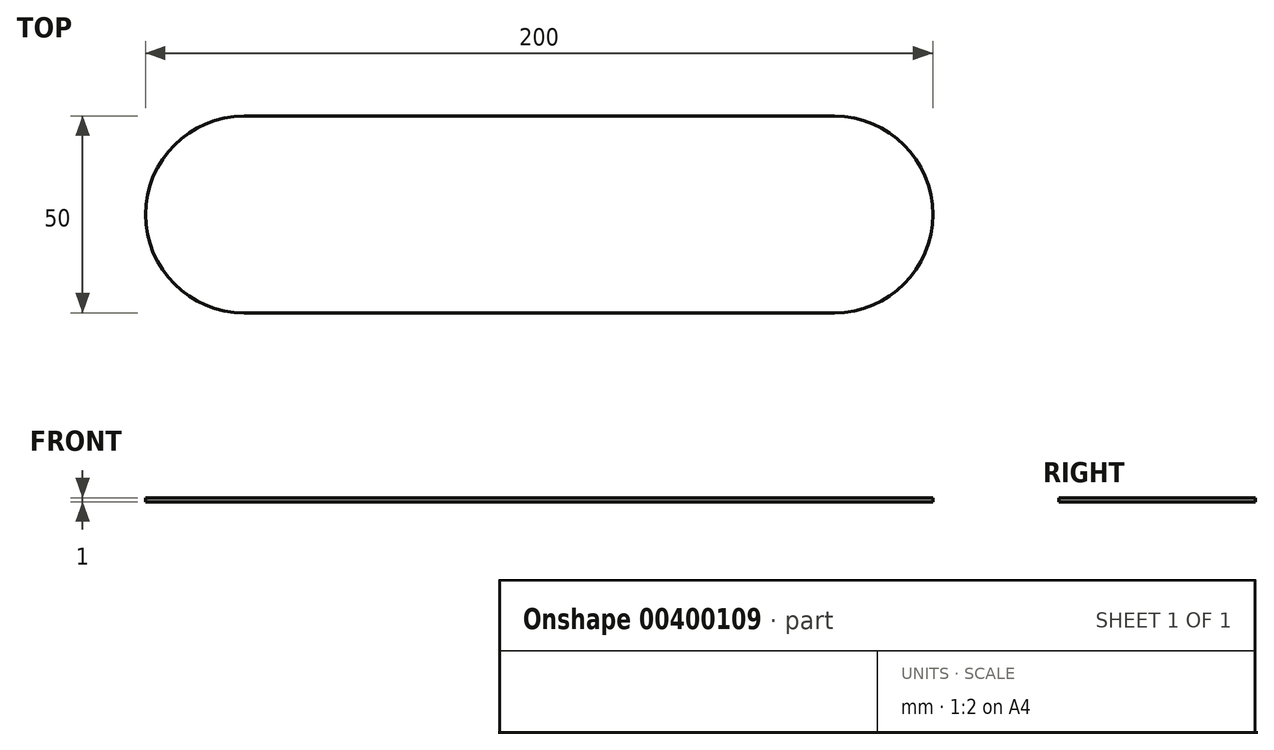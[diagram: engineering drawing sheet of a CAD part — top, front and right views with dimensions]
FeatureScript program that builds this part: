
annotation { "Feature Type Name" : "Feature", "Feature Type Description" : "" }
export const myFeature = defineFeature(function(context is Context, id is Id, definition is map)
    precondition{}
    {
        {
            var Q0;
            Q0=qCreatedBy(makeId("Top.planeOp"),FACE);
            var sketch = newSketch(context, id + "F0", { "sketchPlane" : qUnion([Q0])});
            skLineSegment(sketch, "E0.bottom", {"start": v(75, -25) * mm, "end": v(-75, -25) * mm});
            skLineSegment(sketch, "E0.top", {"start": v(75, 25) * mm, "end": v(-75, 25) * mm});
            skLineSegment(sketch, "E0.left", {"start": v(100, 0) * mm, "end": v(100, 0) * mm});
            skLineSegment(sketch, "E0.right", {"start": v(-100, 0) * mm, "end": v(-100, 0) * mm});
            skPoint(sketch, "E0.middle", {"position": v(0, 0) * mm});
            skPoint(sketch, "E1.visualSharp", {"position": v(-100, -25) * mm});
            skArc(sketch, "E1.filletArc", {"start": v(-100, 0) * mm, "mid": v(-92.68, -17.68) * mm, "end": v(-75, -25) * mm});
            skPoint(sketch, "E2.visualSharp", {"position": v(-100, 25) * mm});
            skArc(sketch, "E2.filletArc", {"start": v(-75, 25) * mm, "mid": v(-92.68, 17.68) * mm, "end": v(-100, 0) * mm});
            skPoint(sketch, "E3.visualSharp", {"position": v(100, -25) * mm});
            skArc(sketch, "E3.filletArc", {"start": v(75, -25) * mm, "mid": v(92.68, -17.68) * mm, "end": v(100, 0) * mm});
            skPoint(sketch, "E4.visualSharp", {"position": v(100, 25) * mm});
            skArc(sketch, "E4.filletArc", {"start": v(100, 0) * mm, "mid": v(92.68, 17.68) * mm, "end": v(75, 25) * mm});
            skSolve(sketch);
        }
        {
            var Q0;
            Q0 = qSketchRegion(id + "F0", true);
            extrude(context, id + "F1", {"entities" : qUnion([Q0]), "depth" : 1 * mm});
        }
    });
